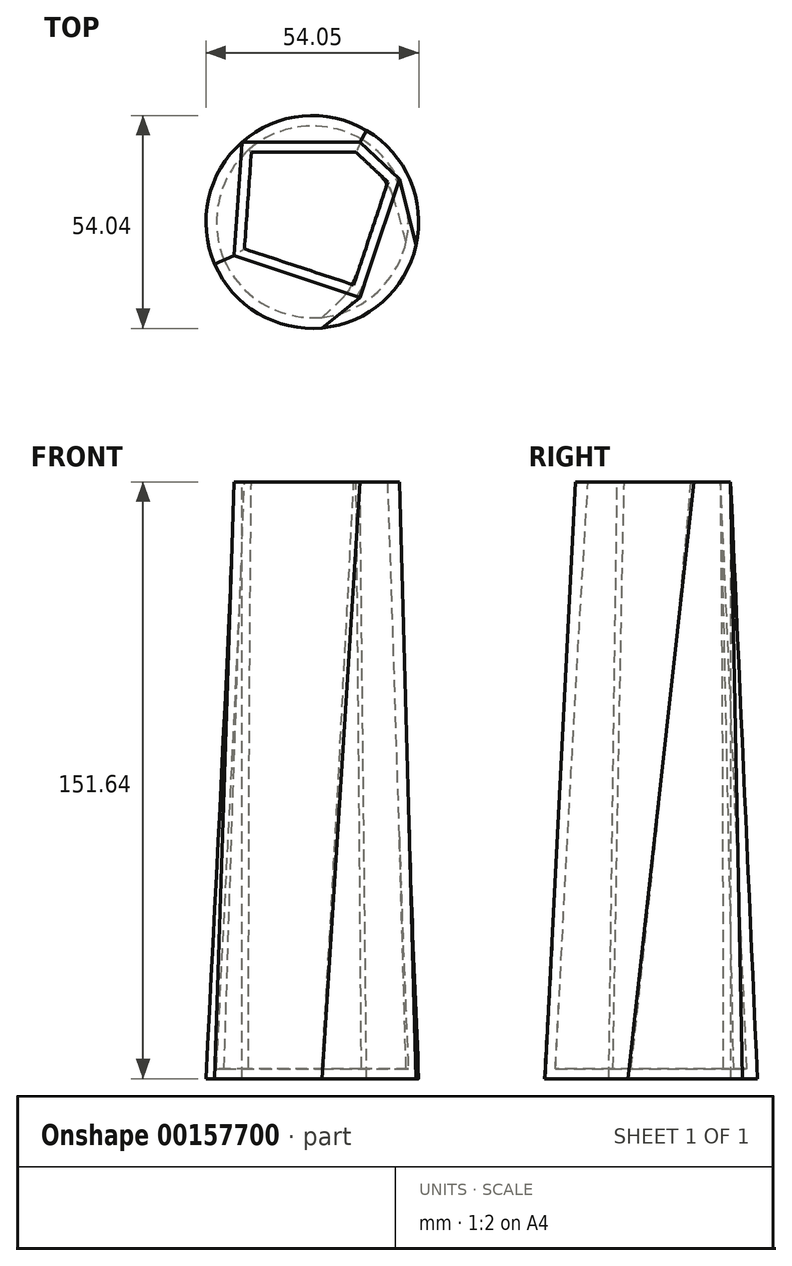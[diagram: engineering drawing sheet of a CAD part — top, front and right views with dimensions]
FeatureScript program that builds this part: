
annotation { "Feature Type Name" : "Feature", "Feature Type Description" : "" }
export const myFeature = defineFeature(function(context is Context, id is Id, definition is map)
    precondition{}
    {
        {
            var Q0;
            Q0=qCreatedBy(makeId("Top.planeOp"),FACE);
            var sketch = newSketch(context, id + "F0", { "sketchPlane" : qUnion([Q0])});
            skCircle(sketch, "E0", {"center": v(1.81, 0) * mm, "radius": 27.02 * mm});
            skSolve(sketch);
        }
        {
            var Q0;
            Q0=makeQuery(id+"F0.imprint","IMPRINT",FACE,{"disambiguationData":[TD([[makeQuery(id+"F0.imprint","IMPRINT",EDGE,{"derivedFrom":sQuery(id+"F0.wireOp",EDGE,"E0")}),1.0]])]});
            cPlane(context, id + "F1", {"entities" : qUnion([Q0]), "cplaneType" : CPlaneType.OFFSET, "offset" : 151.64 * mm, "width" : 152.4 * mm, "height" : 152.4 * mm});
        }
        {
            var Q0;
            Q0=qCreatedBy(id+"F1.planeOp",FACE);
            var sketch = newSketch(context, id + "F2", { "sketchPlane" : qUnion([Q0])});
            skLineSegment(sketch, "E1", {"start": v(-18.12, -8.6) * mm, "end": v(13.92, -19.22) * mm});
            skLineSegment(sketch, "E2", {"start": v(13.92, -19.22) * mm, "end": v(23.91, 10.91) * mm});
            skLineSegment(sketch, "E3", {"start": v(23.91, 10.91) * mm, "end": v(13.92, 20.23) * mm});
            skLineSegment(sketch, "E4", {"start": v(13.92, 20.23) * mm, "end": v(-16.05, 20.23) * mm});
            skLineSegment(sketch, "E5", {"start": v(-16.05, 20.23) * mm, "end": v(-18.12, -8.6) * mm});
            skSolve(sketch);
        }
        {
            var Q0;
            Q0=makeQuery(id+"F0.imprint","IMPRINT",FACE,{"disambiguationData":[TD([[makeQuery(id+"F0.imprint","IMPRINT",EDGE,{"derivedFrom":sQuery(id+"F0.wireOp",EDGE,"E0")}),1.0]])]});
            var Q1;
            Q1=makeQuery(id+"F2.imprint","IMPRINT",FACE,{"disambiguationData":[TD([[makeQuery(id+"F2.imprint","IMPRINT",EDGE,{"derivedFrom":sQuery(id+"F2.wireOp",EDGE,"E1")}),1.0]])]});
            loft(context, id + "F3", {"sheetProfilesArray" : [{ "sheetProfileEntities" : qUnion([Q0]) }, { "sheetProfileEntities" : qUnion([Q1]) }]});
        }
        {
            var Q0;
            Q0=makeQuery(id+"F3.opLoft","CAP_FACE",FACE,{"disambiguationData":[OSD([makeQuery(id+"F2.imprint","IMPRINT",FACE,{"disambiguationData":[TD([[makeQuery(id+"F2.imprint","IMPRINT",EDGE,{"derivedFrom":sQuery(id+"F2.wireOp",EDGE,"E1")}),1.0]])]})])],"isStart":true});
            shell(context, id + "F4", {"entities" : qUnion([Q0]), "thickness" : 2.54 * mm});
        }
    });
